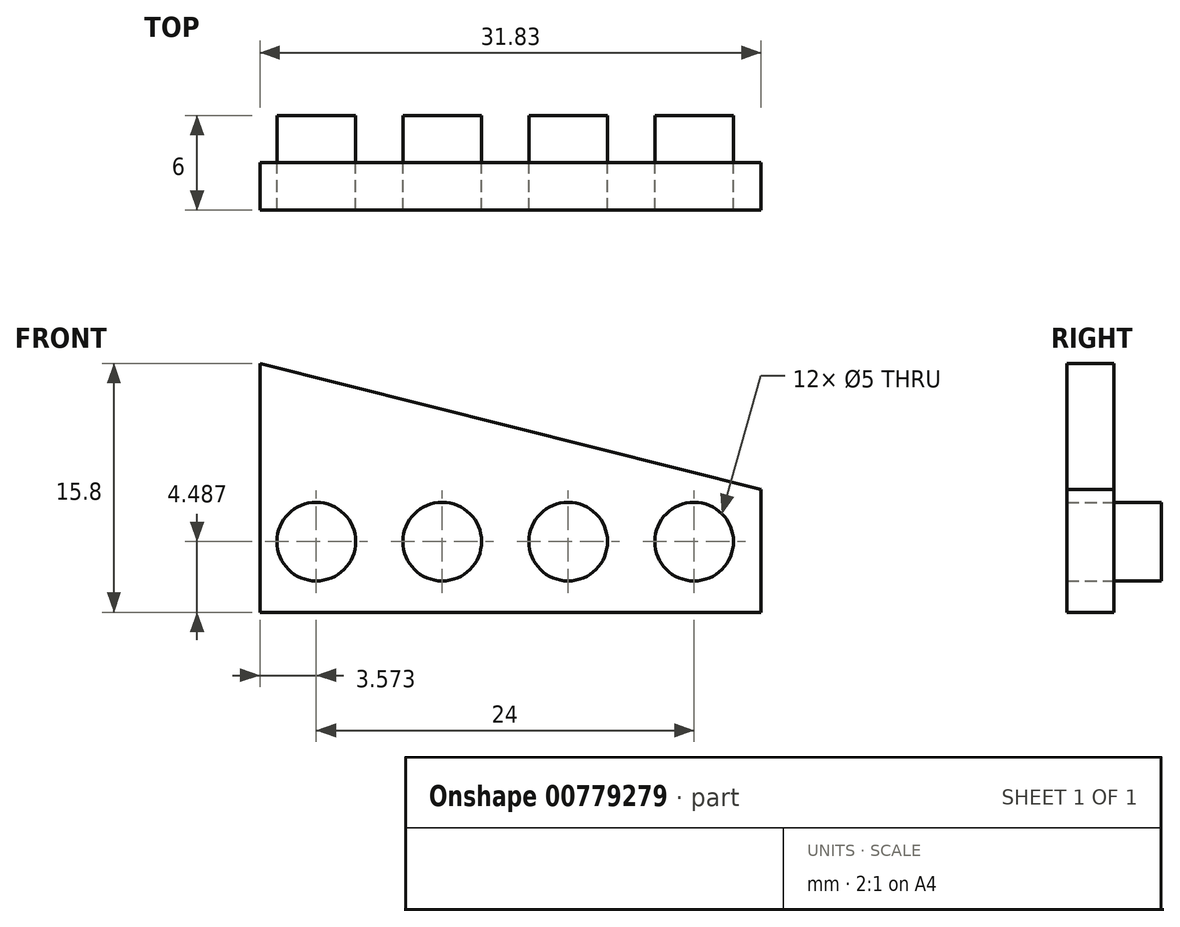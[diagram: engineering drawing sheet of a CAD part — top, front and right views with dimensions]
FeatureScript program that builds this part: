
annotation { "Feature Type Name" : "Feature", "Feature Type Description" : "" }
export const myFeature = defineFeature(function(context is Context, id is Id, definition is map)
    precondition{}
    {
        {
            var Q0;
            Q0=qCreatedBy(makeId("Front.planeOp"),FACE);
            var sketch = newSketch(context, id + "F0", { "sketchPlane" : qUnion([Q0])});
            skLineSegment(sketch, "E0", {"start": v(-23.1, 0) * mm, "end": v(-23.1, 15.8) * mm});
            skLineSegment(sketch, "E1", {"start": v(-23.1, 15.8) * mm, "end": v(8.73, 7.8) * mm});
            skLineSegment(sketch, "E2", {"start": v(8.73, 7.8) * mm, "end": v(8.73, 0) * mm});
            skLineSegment(sketch, "E3", {"start": v(8.73, 0) * mm, "end": v(-23.1, 0) * mm});
            skCircle(sketch, "E4", {"center": v(-19.53, 4.49) * mm, "radius": 2.5 * mm});
            skCircle(sketch, "E5.1.0.0", {"center": v(-11.53, 4.49) * mm, "radius": 2.5 * mm});
            skCircle(sketch, "E5.2.0.0", {"center": v(-3.53, 4.49) * mm, "radius": 2.5 * mm});
            skCircle(sketch, "E5.3.0.0", {"center": v(4.47, 4.49) * mm, "radius": 2.5 * mm});
            skLineSegment(sketch, "E5.direction1", {"start": v(-19.53, 4.49) * mm, "end": v(-11.53, 4.49) * mm, "construction": true});
            skSolve(sketch);
        }
        {
            var Q0;
            Q0=makeQuery(id+"F0.imprint","IMPRINT",FACE,{"disambiguationData":[TD([[makeQuery(id+"F0.imprint","IMPRINT",EDGE,{"derivedFrom":sQuery(id+"F0.wireOp",EDGE,"E0")}),-1.0]])]});
            extrude(context, id + "F1", {"entities" : qUnion([Q0]), "depth" : 3 * mm, "offsetDistance" : 25 * mm});
        }
        {
            var Q0;
            Q0=makeQuery(id+"F0.imprint","IMPRINT",FACE,{"disambiguationData":[TD([[makeQuery(id+"F0.imprint","IMPRINT",EDGE,{"derivedFrom":sQuery(id+"F0.wireOp",EDGE,"E4")}),1.0]])]});
            var Q1;
            Q1=makeQuery(id+"F0.imprint","IMPRINT",FACE,{"disambiguationData":[TD([[makeQuery(id+"F0.imprint","IMPRINT",EDGE,{"derivedFrom":sQuery(id+"F0.wireOp",EDGE,"E5.1.0.0")}),1.0]])]});
            var Q2;
            Q2=makeQuery(id+"F0.imprint","IMPRINT",FACE,{"disambiguationData":[TD([[makeQuery(id+"F0.imprint","IMPRINT",EDGE,{"derivedFrom":sQuery(id+"F0.wireOp",EDGE,"E5.2.0.0")}),1.0]])]});
            var Q3;
            Q3=makeQuery(id+"F0.imprint","IMPRINT",FACE,{"disambiguationData":[TD([[makeQuery(id+"F0.imprint","IMPRINT",EDGE,{"derivedFrom":sQuery(id+"F0.wireOp",EDGE,"E5.3.0.0")}),1.0]])]});
            extrude(context, id + "F2", {"entities" : qUnion([Q0, Q1, Q2, Q3]), "oppositeDirection" : true, "depth" : 3 * mm, "offsetDistance" : 25 * mm});
        }
    });
